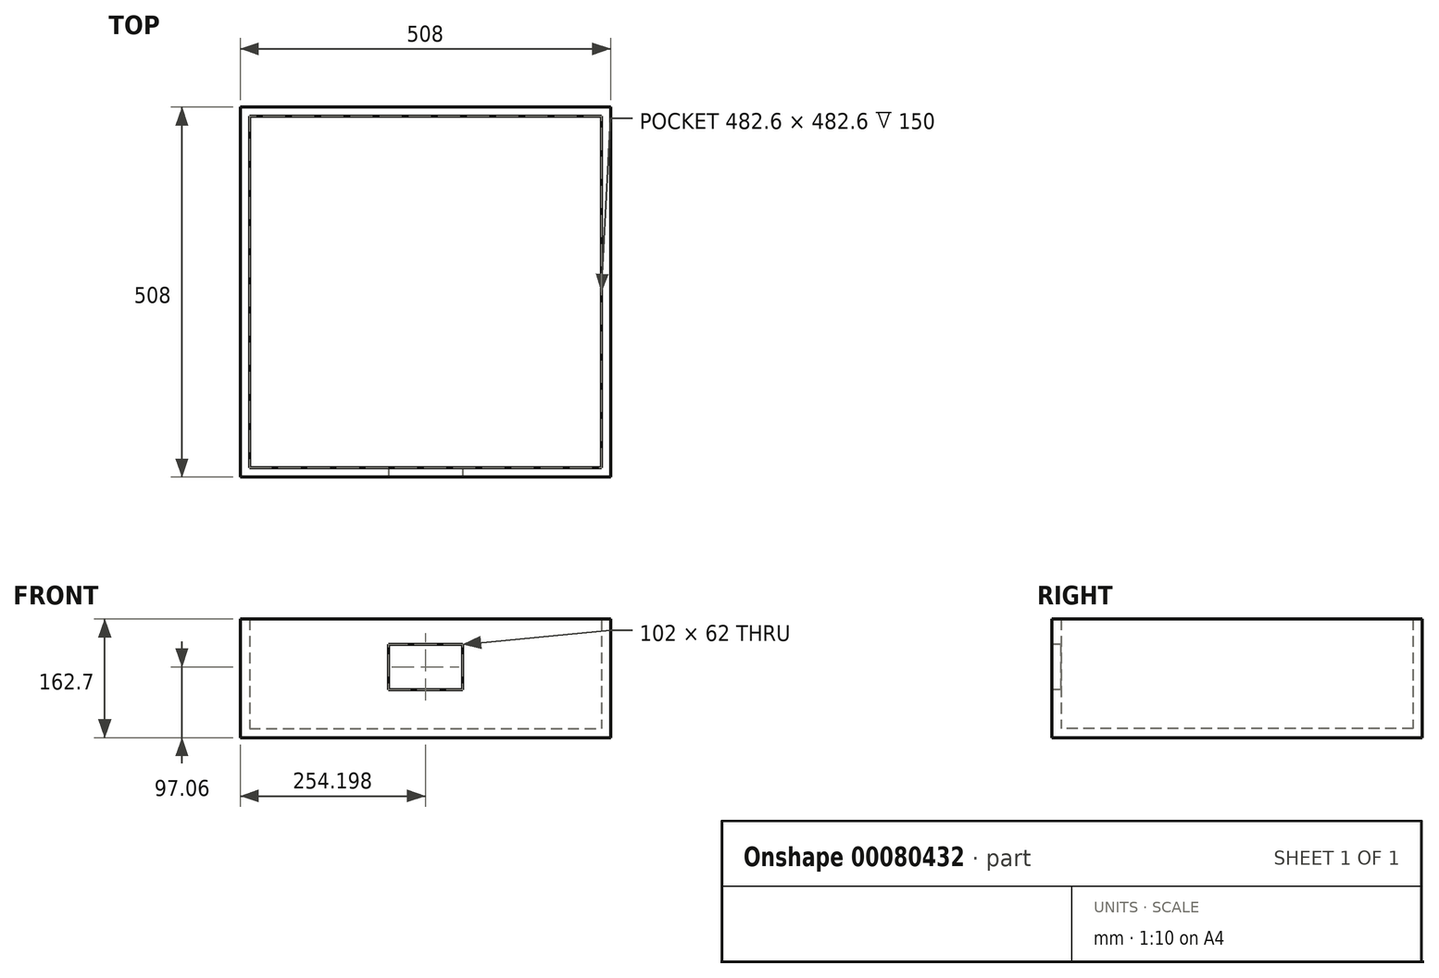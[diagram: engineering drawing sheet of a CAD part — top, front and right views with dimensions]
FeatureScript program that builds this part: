
annotation { "Feature Type Name" : "Feature", "Feature Type Description" : "" }
export const myFeature = defineFeature(function(context is Context, id is Id, definition is map)
    precondition{}
    {
        {
            var Q0;
            Q0=qCreatedBy(makeId("Top.planeOp"),FACE);
            var sketch = newSketch(context, id + "F0", { "sketchPlane" : qUnion([Q0])});
            skLineSegment(sketch, "E0.bottom", {"start": v(254, -254) * mm, "end": v(-254, -254) * mm});
            skLineSegment(sketch, "E0.top", {"start": v(254, 254) * mm, "end": v(-254, 254) * mm});
            skLineSegment(sketch, "E0.left", {"start": v(254, -254) * mm, "end": v(254, 254) * mm});
            skLineSegment(sketch, "E0.right", {"start": v(-254, -254) * mm, "end": v(-254, 254) * mm});
            skPoint(sketch, "E0.middle", {"position": v(0, 0) * mm});
            skSolve(sketch);
        }
        {
            var Q0;
            Q0=makeQuery(id+"F0.imprint","IMPRINT",FACE,{"disambiguationData":[TD([[makeQuery(id+"F0.imprint","IMPRINT",EDGE,{"derivedFrom":sQuery(id+"F0.wireOp",EDGE,"E0.bottom")}),-1.0]])]});
            extrude(context, id + "F1", {"entities" : qUnion([Q0]), "oppositeDirection" : true, "depth" : 12.7 * mm});
        }
        {
            var Q0;
            Q0=makeQuery(id+"F1.opExtrude","CAP_FACE",FACE,{"disambiguationData":[OSD([sQuery(id+"F0.wireOp",EDGE,"E0.bottom"),sQuery(id+"F0.wireOp",EDGE,"E0.top"),sQuery(id+"F0.wireOp",EDGE,"E0.left"),sQuery(id+"F0.wireOp",EDGE,"E0.right")])],"isStart":true});
            var sketch = newSketch(context, id + "F2", { "sketchPlane" : qUnion([Q0])});
            skLineSegment(sketch, "E1.bottom", {"start": v(-254, 254) * mm, "end": v(254, 254) * mm});
            skLineSegment(sketch, "E1.top", {"start": v(-241.3, 241.3) * mm, "end": v(241.3, 241.3) * mm});
            skLineSegment(sketch, "E1.left", {"start": v(-254, 254) * mm, "end": v(-254, 241.3) * mm});
            skLineSegment(sketch, "E1.right", {"start": v(254, 254) * mm, "end": v(254, 241.3) * mm});
            skLineSegment(sketch, "E2.bottom", {"start": v(-254, 254) * mm, "end": v(-241.3, 254) * mm});
            skLineSegment(sketch, "E2.top", {"start": v(-254, -254) * mm, "end": v(-241.3, -254) * mm});
            skLineSegment(sketch, "E2.left", {"start": v(-254, 254) * mm, "end": v(-254, -254) * mm});
            skLineSegment(sketch, "E2.right", {"start": v(-241.3, 241.3) * mm, "end": v(-241.3, -241.3) * mm});
            skLineSegment(sketch, "E3.top", {"start": v(-254, -254) * mm, "end": v(254, -254) * mm});
            skLineSegment(sketch, "E3.left", {"start": v(-254, -233.08) * mm, "end": v(-254, -254) * mm});
            skLineSegment(sketch, "E3.right", {"start": v(254, -241.3) * mm, "end": v(254, -254) * mm});
            skLineSegment(sketch, "E4.bottom", {"start": v(254, -254) * mm, "end": v(241.3, -254) * mm});
            skLineSegment(sketch, "E4.top", {"start": v(254, 254) * mm, "end": v(241.3, 254) * mm});
            skLineSegment(sketch, "E4.left", {"start": v(254, -254) * mm, "end": v(254, 254) * mm});
            skLineSegment(sketch, "E4.right", {"start": v(241.3, -241.3) * mm, "end": v(241.3, 241.3) * mm});
            skLineSegment(sketch, "E5.top", {"start": v(-241.3, -241.3) * mm, "end": v(241.3, -241.3) * mm});
            skLineSegment(sketch, "E5.left", {"start": v(-254, -254) * mm, "end": v(-254, -241.3) * mm});
            skLineSegment(sketch, "E5.right", {"start": v(309.14, -254) * mm, "end": v(309.14, -241.3) * mm});
            skSolve(sketch);
        }
        {
            var Q0;
            Q0=makeQuery(id+"F2.imprint","IMPRINT",FACE,{"disambiguationData":[TD([[makeQuery(id+"F2.imprint","IMPRINT",EDGE,{"derivedFrom":sQuery(id+"F2.wireOp",EDGE,"E1.bottom")}),1.0]])]});
            extrude(context, id + "F3", {"entities" : qUnion([Q0]), "operationType" : NewBodyOperationType.ADD, "depth" : 150 * mm});
        }
        {
            var Q0;
            Q0=makeQuery(id+"F3.boolean.opBoolean","MERGE",FACE,{"derivedFrom":[makeQuery(id+"F1.opExtrude","SWEPT_FACE",FACE,{"disambiguationData":[OSD([sQuery(id+"F0.wireOp",EDGE,"E0.bottom")])]}),makeQuery(id+"F3.opExtrude","SWEPT_FACE",FACE,{"disambiguationData":[OSD([sQuery(id+"F2.wireOp",EDGE,"E3.top")])]})]});
            var sketch = newSketch(context, id + "F4", { "sketchPlane" : qUnion([Q0])});
            skLineSegment(sketch, "E6.bottom", {"start": v(-50.8, 115.36) * mm, "end": v(51.2, 115.36) * mm});
            skLineSegment(sketch, "E6.top", {"start": v(-50.8, 53.36) * mm, "end": v(51.2, 53.36) * mm});
            skLineSegment(sketch, "E6.left", {"start": v(-50.8, 115.36) * mm, "end": v(-50.8, 53.36) * mm});
            skLineSegment(sketch, "E6.right", {"start": v(51.2, 115.36) * mm, "end": v(51.2, 53.36) * mm});
            skSolve(sketch);
        }
        {
            var Q0;
            Q0=makeQuery(id+"F4.imprint","IMPRINT",FACE,{"disambiguationData":[TD([[makeQuery(id+"F4.imprint","IMPRINT",EDGE,{"derivedFrom":sQuery(id+"F4.wireOp",EDGE,"E6.bottom")}),-1.0]])]});
            extrude(context, id + "F5", {"entities" : qUnion([Q0]), "operationType" : NewBodyOperationType.REMOVE, "oppositeDirection" : true, "depth" : 50.8 * mm});
        }
    });
